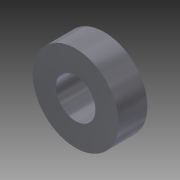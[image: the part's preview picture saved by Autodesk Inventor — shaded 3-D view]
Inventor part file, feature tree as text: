
AUTODESK INVENTOR PART (.ipt)
format: ipt  version: 2012 (Build 160160000, 160)  size: 79,360 bytes
history: native  units: in
note: dims shown in document units (in); Inventor stores cm internally (conversion verified against a paired STEP export)
features: extrude x1, sketch x1
ambient origin geometry x8: Origin, YZ Plane, XZ Plane, XY Plane, X Axis, Y Axis, Z Axis, Center Point
bodies: Solid1 (feature_tree)
feature tree (2):
  extrude  "Extrusion1"  Depth=0.3447in
  sketch  "Sketch1"  dims[d0=0.75in d1=0.3447in d2=0.25in d3=0.0in]
